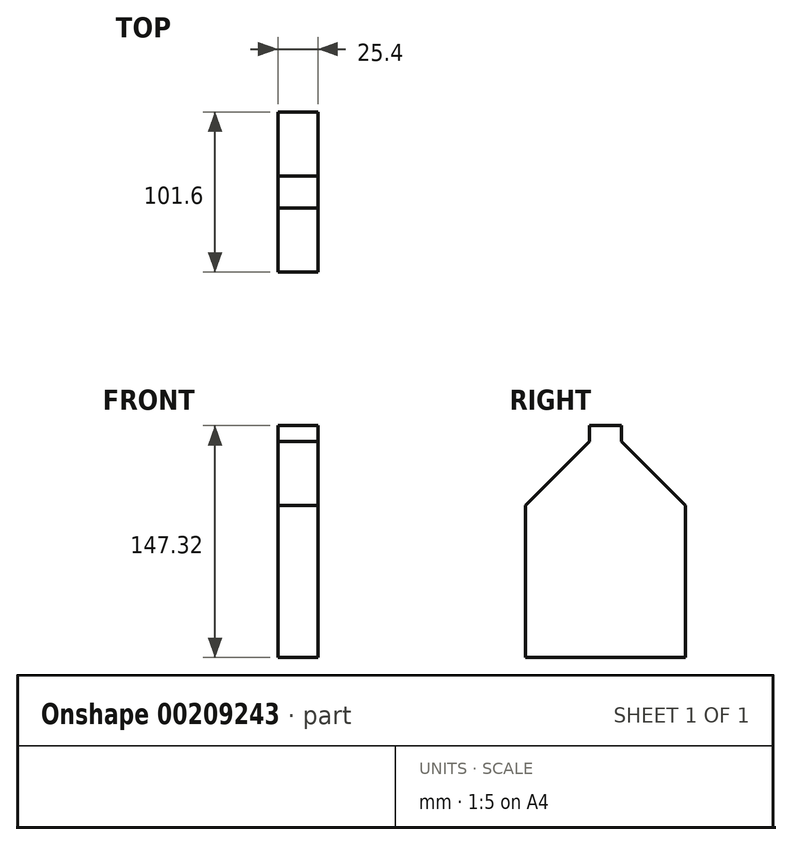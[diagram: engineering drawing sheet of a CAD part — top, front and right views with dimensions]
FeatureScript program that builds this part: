
annotation { "Feature Type Name" : "Feature", "Feature Type Description" : "" }
export const myFeature = defineFeature(function(context is Context, id is Id, definition is map)
    precondition{}
    {
        {
            var Q0;
            Q0=qCreatedBy(makeId("Right.planeOp"),FACE);
            var sketch = newSketch(context, id + "F0", { "sketchPlane" : qUnion([Q0])});
            skLineSegment(sketch, "E0.top", {"start": v(-50.8, -75.62) * mm, "end": v(50.8, -75.62) * mm});
            skLineSegment(sketch, "E0.left", {"start": v(-50.8, 20.9) * mm, "end": v(-50.8, -75.62) * mm});
            skLineSegment(sketch, "E0.right", {"start": v(50.8, 20.9) * mm, "end": v(50.8, -75.62) * mm});
            skPoint(sketch, "E0.middle", {"position": v(0, -27.36) * mm});
            skLineSegment(sketch, "E1", {"start": v(50.8, 20.9) * mm, "end": v(10.16, 61.54) * mm});
            skLineSegment(sketch, "E2", {"start": v(10.16, 61.54) * mm, "end": v(10.16, 71.7) * mm});
            skLineSegment(sketch, "E3", {"start": v(10.16, 71.7) * mm, "end": v(0, 71.7) * mm});
            skLineSegment(sketch, "E4.MirrorCS", {"start": v(-10.16, 71.7) * mm, "end": v(0, 71.7) * mm});
            skLineSegment(sketch, "E5.MirrorCS", {"start": v(-10.16, 61.54) * mm, "end": v(-10.16, 71.7) * mm});
            skLineSegment(sketch, "E6.MirrorCS", {"start": v(-50.8, 20.9) * mm, "end": v(-10.16, 61.54) * mm});
            skSolve(sketch);
        }
        {
            var Q0;
            Q0=makeQuery(id+"F0.imprint","IMPRINT",FACE,{"disambiguationData":[TD([[makeQuery(id+"F0.imprint","IMPRINT",EDGE,{"derivedFrom":sQuery(id+"F0.wireOp",EDGE,"E0.top")}),1.0]])]});
            extrude(context, id + "F1", {"entities" : qUnion([Q0]), "endBound" : BoundingType.SYMMETRIC, "depth" : 25.4 * mm});
        }
    });
